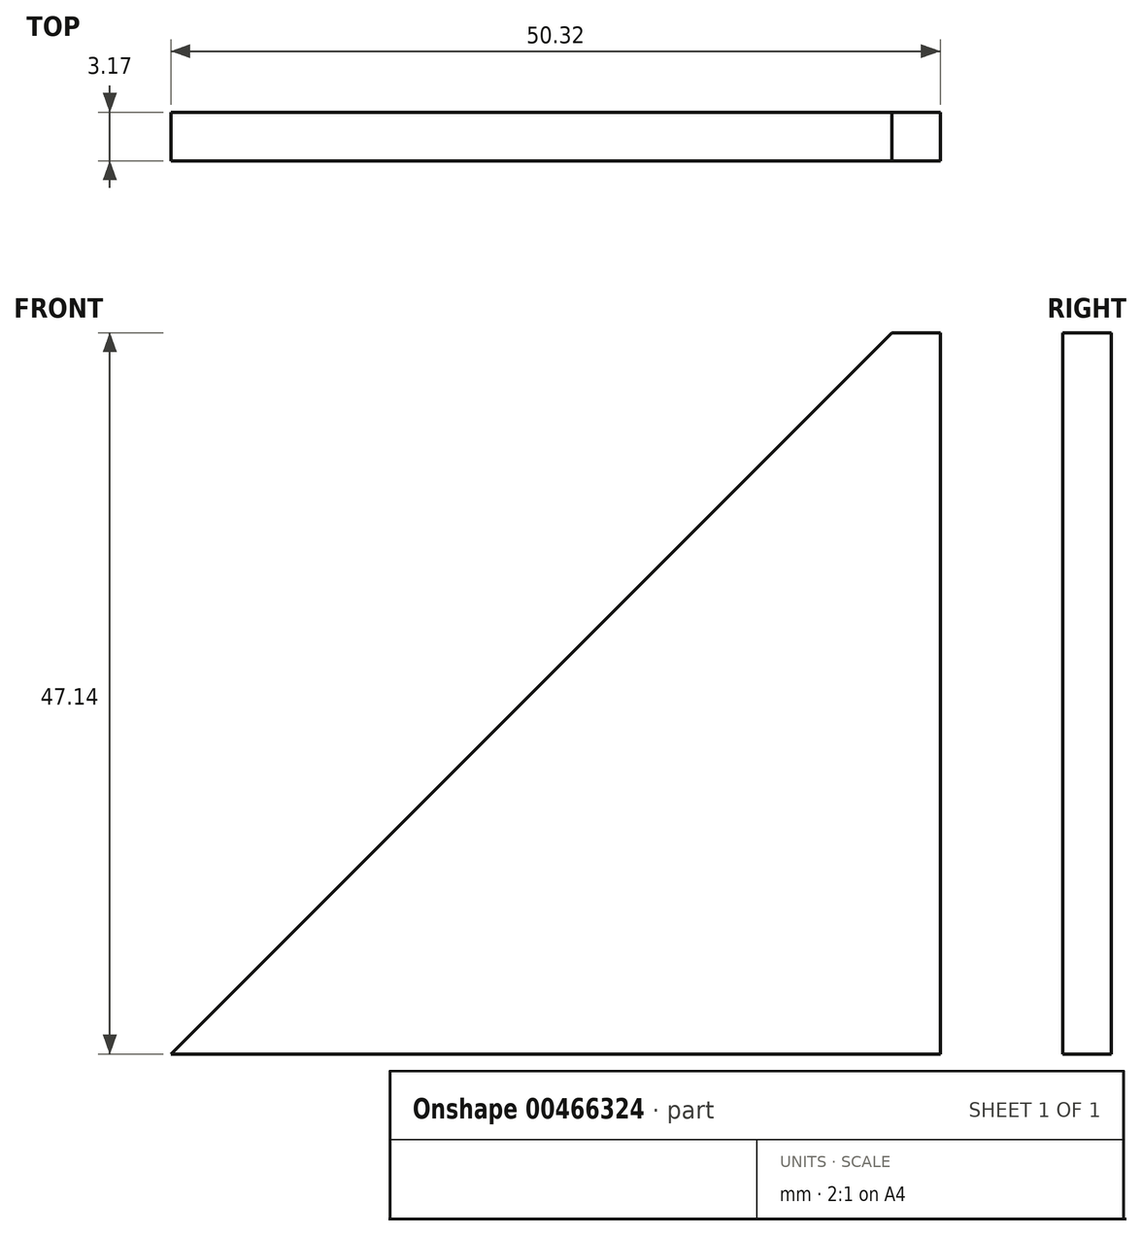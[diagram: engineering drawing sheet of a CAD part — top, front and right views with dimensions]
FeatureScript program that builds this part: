
annotation { "Feature Type Name" : "Feature", "Feature Type Description" : "" }
export const myFeature = defineFeature(function(context is Context, id is Id, definition is map)
    precondition{}
    {
        {
            var Q0;
            Q0=qCreatedBy(makeId("Front.planeOp"),FACE);
            var sketch = newSketch(context, id + "F0", { "sketchPlane" : qUnion([Q0])});
            skLineSegment(sketch, "E0", {"start": v(-40.91, 2.55) * mm, "end": v(6.23, 49.7) * mm});
            skLineSegment(sketch, "E1", {"start": v(-40.91, 2.55) * mm, "end": v(6.23, 2.55) * mm});
            skLineSegment(sketch, "E2", {"start": v(6.23, 49.7) * mm, "end": v(6.23, 2.55) * mm});
            skLineSegment(sketch, "E3", {"start": v(6.23, 49.7) * mm, "end": v(9.4, 49.7) * mm});
            skLineSegment(sketch, "E4", {"start": v(6.23, 2.55) * mm, "end": v(9.4, 2.55) * mm});
            skLineSegment(sketch, "E5", {"start": v(9.4, 2.55) * mm, "end": v(9.4, 49.7) * mm});
            skSolve(sketch);
        }
        {
            var Q0;
            Q0=makeQuery(id+"F0.imprint","IMPRINT",FACE,{"disambiguationData":[TD([[makeQuery(id+"F0.imprint","IMPRINT",EDGE,{"derivedFrom":sQuery(id+"F0.wireOp",EDGE,"E0")}),-1.0]])]});
            var Q1;
            Q1=makeQuery(id+"F0.imprint","IMPRINT",FACE,{"disambiguationData":[TD([[makeQuery(id+"F0.imprint","IMPRINT",EDGE,{"derivedFrom":sQuery(id+"F0.wireOp",EDGE,"E2")}),1.0]])]});
            extrude(context, id + "F1", {"entities" : qUnion([Q0, Q1]), "depth" : 3.17 * mm});
        }
    });
